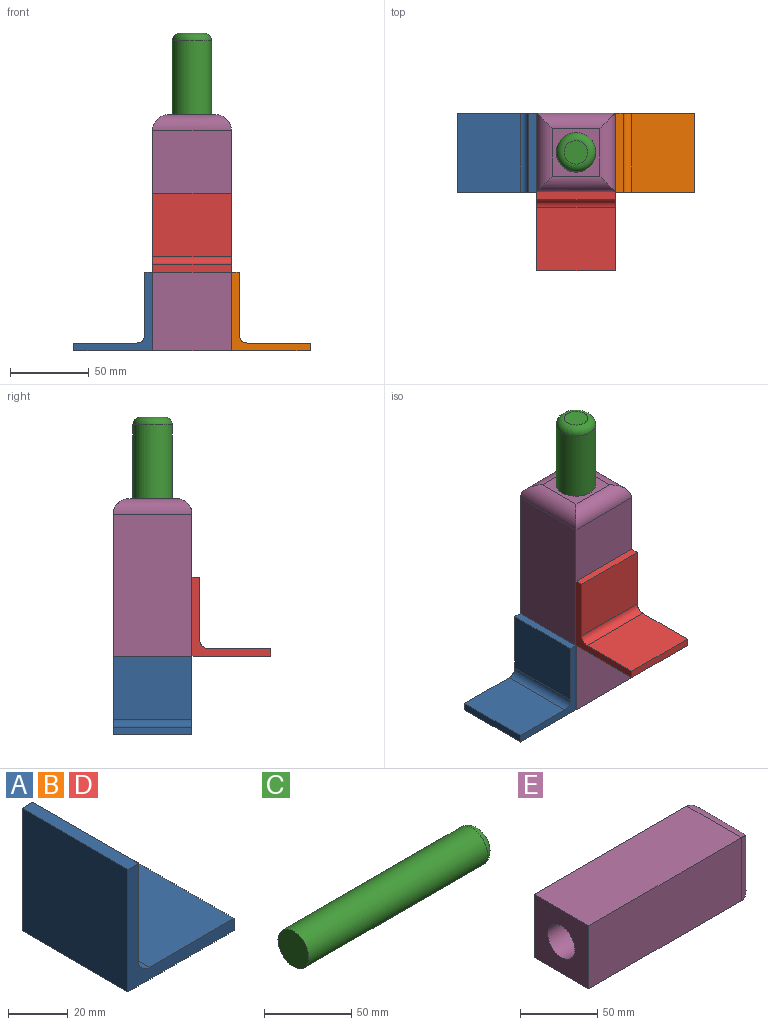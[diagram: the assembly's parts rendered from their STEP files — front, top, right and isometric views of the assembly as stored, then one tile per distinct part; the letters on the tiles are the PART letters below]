
ASSEMBLY  parts=5 mates=4
PART A: 9 faces, bbox 50x50x50 mm
  f0: plane 50x5mm, normal (0,0,1), area 250mm2, adj f1,f6,f7,f8
  f1: plane 50x50mm, normal (-1,0,0), area 2500mm2, adj f0,f2,f7,f8
  f2: plane 50x50mm, normal (0,0,-1), area 2500mm2, adj f1,f3,f7,f8
  f3: plane 50x5mm, normal (1,0,0), area 250mm2, adj f2,f4,f7,f8
  f4: plane 50x40mm, normal (0,0,1), area 2000mm2, adj f3,f5,f7,f8
  f5: cylinder r=5mm len=50mm, axis (0,1,0), area 392.7mm2, adj f4,f6,f7,f8
  f6: plane 50x40mm, normal (1,0,0), area 2000mm2, adj f0,f5,f7,f8
  f7: plane 50x50mm, normal (0,-1,0), area 480.4mm2, adj f0,f1,f2,f3,f4,f5,f6
  f8: plane 50x50mm, normal (0,1,0), area 480.4mm2, adj f0,f1,f2,f3,f4,f5,f6
PART B: same geometry as A
PART C: 4 faces, bbox 150x27x27 mm
  f0: cylinder r=12.47mm len=145mm, axis (-1,0,0), area 11365.5mm2, adj f2,f3
  f1: plane 14.95x14.95mm, normal (1,0,0), area 175.5mm2, adj f3
  f2: plane 24.95x24.95mm, normal (-1,0,0), area 488.9mm2, adj f0
  f3: torus R=7.47mm, axis (1,0,0), area 526mm2, adj f0,f1
PART D: same geometry as A
PART E: 11 faces, bbox 150x50x50 mm
  f0: plane 50x50mm, normal (-1,0,0), area 2009.1mm2, adj f1,f3,f4,f5,f6
  f1: plane 140x50mm, normal (0,-1,0), area 7000mm2, adj f0,f4,f5,f10
  f2: plane 30x30mm, normal (1,0,0), area 409.1mm2, adj f6,f7,f8,f9,f10
  f3: plane 140x50mm, normal (0,1,0), area 7000mm2, adj f0,f4,f5,f7
  f4: plane 140x50mm, normal (0,0,1), area 7000mm2, adj f0,f1,f3,f8
  f5: plane 140x50mm, normal (0,0,-1), area 7000mm2, adj f0,f1,f3,f9
  f6: cylinder r=12.5mm len=150mm, axis (1,0,0), area 11781mm2, adj f0,f2
  f7: cylinder r=10mm len=50mm, axis (0,0,-1), area 671.2mm2, adj f2,f3,f8,f9
  f8: cylinder r=10mm len=50mm, axis (0,-1,0), area 671.2mm2, adj f2,f4,f7,f10
  f9: cylinder r=10mm len=50mm, axis (0,1,0), area 671.2mm2, adj f2,f5,f7,f10
  f10: cylinder r=10mm len=50mm, axis (0,0,-1), area 671.2mm2, adj f1,f2,f8,f9
PLACE A rot(axis=(0,0,1),180deg) t=(-16.79,0,0)mm
PLACE B rot(axis=(-0.71,0,-0.71),180deg) t=(50,0,16.79)mm
PLACE C rot(axis=(0,-1,0),90deg) t=(25,25,51.76)mm
PLACE D rot(axis=(0.58,-0.58,0.58),120deg) t=(0,0,66.79)mm
PLACE E rot(axis=(0,-1,0),90deg) t=(50,0,0)mm
MATE fastened A.f1 <-> E.f4  axis (1,0,0) through (0,25,0)mm
MATE fastened B.f2 <-> E.f5  axis (-1,0,0) through (50,25,0)mm
MATE fastened D.f2 <-> E.f1  axis (0,1,0) through (25,0,50)mm
MATE slider E.f6 <-> C.f0  axis (0,0,1) through (25,25,150)mm
